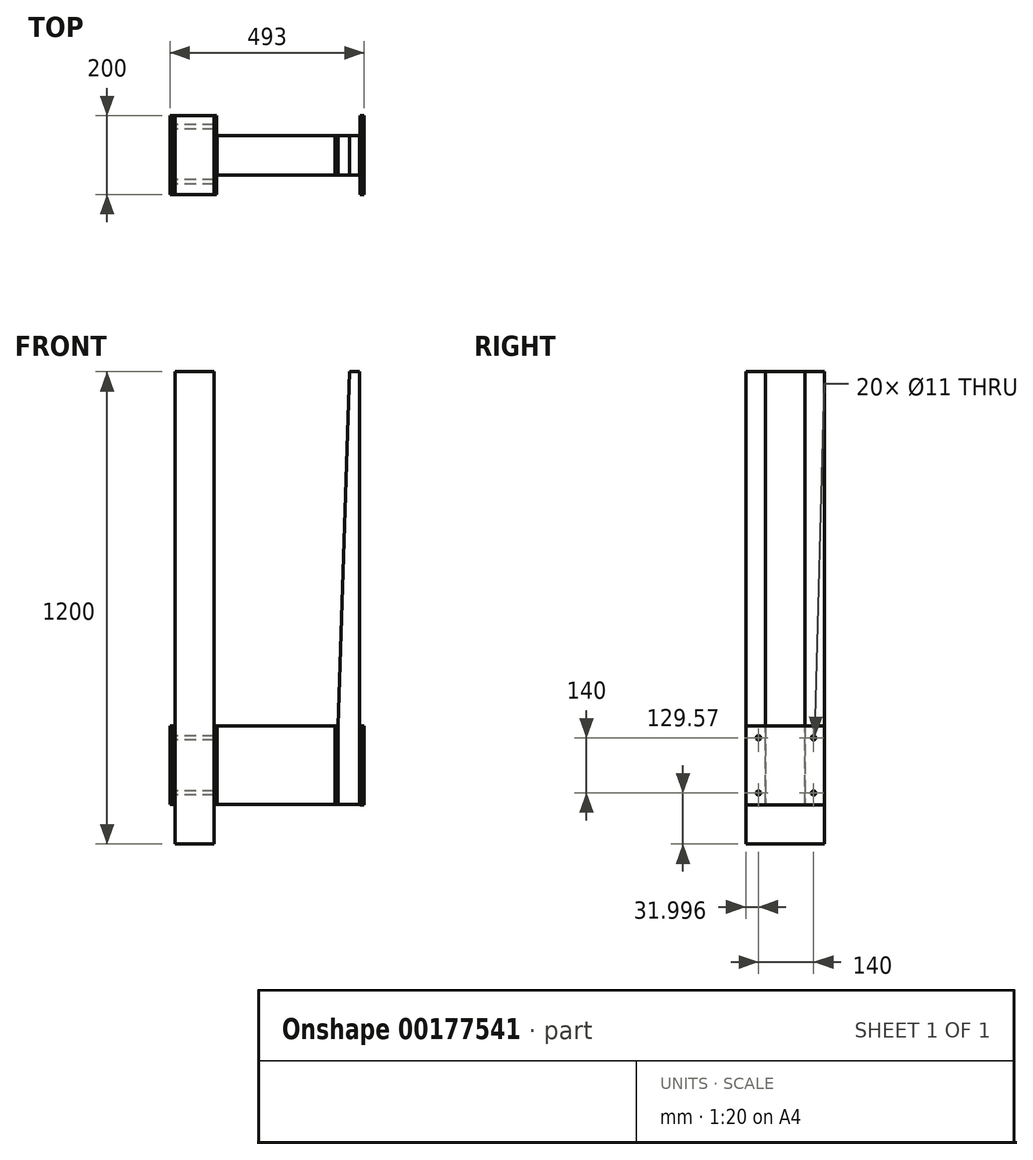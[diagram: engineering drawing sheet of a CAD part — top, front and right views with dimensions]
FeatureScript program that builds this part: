
annotation { "Feature Type Name" : "Feature", "Feature Type Description" : "" }
export const myFeature = defineFeature(function(context is Context, id is Id, definition is map)
    precondition{}
    {
        {
            var Q0;
            Q0=qCreatedBy(makeId("Front.planeOp"),FACE);
            var sketch = newSketch(context, id + "F0", { "sketchPlane" : qUnion([Q0])});
            skLineSegment(sketch, "E0", {"start": v(116.79, 818.01) * mm, "end": v(116.79, -281.99) * mm});
            skLineSegment(sketch, "E1", {"start": v(116.79, -281.99) * mm, "end": v(61.79, -281.99) * mm});
            skLineSegment(sketch, "E2", {"start": v(61.79, -281.99) * mm, "end": v(61.79, -81.99) * mm});
            skLineSegment(sketch, "E3", {"start": v(116.79, 818.01) * mm, "end": v(91.79, 818.01) * mm});
            skLineSegment(sketch, "E4", {"start": v(91.79, 818.01) * mm, "end": v(61.79, -81.99) * mm});
            skLineSegment(sketch, "E5.bottom", {"start": v(-245.21, -81.62) * mm, "end": v(54.79, -81.62) * mm});
            skLineSegment(sketch, "E5.top", {"start": v(-245.21, -281.62) * mm, "end": v(54.79, -281.62) * mm});
            skLineSegment(sketch, "E5.left", {"start": v(54.79, -81.62) * mm, "end": v(54.79, -281.62) * mm});
            skLineSegment(sketch, "E5.right", {"start": v(-245.21, -81.62) * mm, "end": v(-245.21, -281.62) * mm});
            skLineSegment(sketch, "E6.bottom", {"start": v(-352.21, 818.13) * mm, "end": v(-252.21, 818.13) * mm});
            skLineSegment(sketch, "E6.top", {"start": v(-352.21, -381.87) * mm, "end": v(-252.21, -381.87) * mm});
            skLineSegment(sketch, "E6.left", {"start": v(-352.21, 818.13) * mm, "end": v(-352.21, -381.87) * mm});
            skLineSegment(sketch, "E6.right", {"start": v(-252.21, 818.13) * mm, "end": v(-252.21, -381.87) * mm});
            skLineSegment(sketch, "E7.bottom", {"start": v(123.79, -82.45) * mm, "end": v(128.79, -82.45) * mm});
            skLineSegment(sketch, "E7.top", {"start": v(123.79, -282.45) * mm, "end": v(128.79, -282.45) * mm});
            skLineSegment(sketch, "E7.left", {"start": v(123.79, -82.45) * mm, "end": v(123.79, -282.45) * mm});
            skLineSegment(sketch, "E7.right", {"start": v(128.79, -82.45) * mm, "end": v(128.79, -282.45) * mm});
            skLineSegment(sketch, "E8.bottom", {"start": v(-364.21, -81.85) * mm, "end": v(-359.21, -81.85) * mm});
            skLineSegment(sketch, "E8.top", {"start": v(-364.21, -281.85) * mm, "end": v(-359.21, -281.85) * mm});
            skLineSegment(sketch, "E8.left", {"start": v(-364.21, -81.85) * mm, "end": v(-364.21, -281.85) * mm});
            skLineSegment(sketch, "E8.right", {"start": v(-359.21, -81.85) * mm, "end": v(-359.21, -281.85) * mm});
            skLineSegment(sketch, "E9.bottom", {"start": v(-358.21, -281.87) * mm, "end": v(-353.21, -281.87) * mm});
            skLineSegment(sketch, "E9.top", {"start": v(-358.21, -81.87) * mm, "end": v(-353.21, -81.87) * mm});
            skLineSegment(sketch, "E9.left", {"start": v(-358.21, -281.87) * mm, "end": v(-358.21, -81.87) * mm});
            skLineSegment(sketch, "E9.right", {"start": v(-353.21, -281.87) * mm, "end": v(-353.21, -81.87) * mm});
            skLineSegment(sketch, "E10.bottom", {"start": v(-251.21, -281.62) * mm, "end": v(-246.21, -281.62) * mm});
            skLineSegment(sketch, "E10.top", {"start": v(-251.21, -81.62) * mm, "end": v(-246.21, -81.62) * mm});
            skLineSegment(sketch, "E10.left", {"start": v(-251.21, -281.62) * mm, "end": v(-251.21, -81.62) * mm});
            skLineSegment(sketch, "E10.right", {"start": v(-246.21, -281.62) * mm, "end": v(-246.21, -81.62) * mm});
            skLineSegment(sketch, "E11.bottom", {"start": v(117.79, -82.45) * mm, "end": v(122.79, -82.45) * mm});
            skLineSegment(sketch, "E11.top", {"start": v(117.79, -282.45) * mm, "end": v(122.79, -282.45) * mm});
            skLineSegment(sketch, "E11.left", {"start": v(117.79, -82.45) * mm, "end": v(117.79, -282.45) * mm});
            skLineSegment(sketch, "E11.right", {"start": v(122.79, -82.45) * mm, "end": v(122.79, -282.45) * mm});
            skLineSegment(sketch, "E12.bottom", {"start": v(55.79, -81.99) * mm, "end": v(60.79, -81.99) * mm});
            skLineSegment(sketch, "E12.top", {"start": v(55.79, -281.99) * mm, "end": v(60.79, -281.99) * mm});
            skLineSegment(sketch, "E12.left", {"start": v(55.79, -81.99) * mm, "end": v(55.79, -281.99) * mm});
            skLineSegment(sketch, "E12.right", {"start": v(60.79, -81.99) * mm, "end": v(60.79, -281.99) * mm});
            skSolve(sketch);
        }
        {
            var Q0;
            Q0=makeQuery(id+"F0.imprint","IMPRINT",FACE,{"disambiguationData":[TD([[makeQuery(id+"F0.imprint","IMPRINT",EDGE,{"derivedFrom":sQuery(id+"F0.wireOp",EDGE,"E8.bottom")}),-1.0]])]});
            var Q1;
            Q1=makeQuery(id+"F0.imprint","IMPRINT",FACE,{"disambiguationData":[TD([[makeQuery(id+"F0.imprint","IMPRINT",EDGE,{"derivedFrom":sQuery(id+"F0.wireOp",EDGE,"E9.bottom")}),1.0]])]});
            var Q2;
            Q2=makeQuery(id+"F0.imprint","IMPRINT",FACE,{"disambiguationData":[TD([[makeQuery(id+"F0.imprint","IMPRINT",EDGE,{"derivedFrom":sQuery(id+"F0.wireOp",EDGE,"E6.bottom")}),-1.0]])]});
            var Q3;
            Q3=makeQuery(id+"F0.imprint","IMPRINT",FACE,{"disambiguationData":[TD([[makeQuery(id+"F0.imprint","IMPRINT",EDGE,{"derivedFrom":sQuery(id+"F0.wireOp",EDGE,"E10.bottom")}),1.0]])]});
            var Q4;
            Q4=makeQuery(id+"F0.imprint","IMPRINT",FACE,{"disambiguationData":[TD([[makeQuery(id+"F0.imprint","IMPRINT",EDGE,{"derivedFrom":sQuery(id+"F0.wireOp",EDGE,"E7.bottom")}),-1.0]])]});
            var Q5;
            Q5=makeQuery(id+"F0.imprint","IMPRINT",FACE,{"disambiguationData":[TD([[makeQuery(id+"F0.imprint","IMPRINT",EDGE,{"derivedFrom":sQuery(id+"F0.wireOp",EDGE,"E11.bottom")}),-1.0]])]});
            extrude(context, id + "F1", {"entities" : qUnion([Q0, Q1, Q2, Q3, Q4, Q5]), "endBound" : BoundingType.SYMMETRIC, "depth" : 200 * mm});
        }
        {
            var Q0;
            Q0=makeQuery(id+"F0.imprint","IMPRINT",FACE,{"disambiguationData":[TD([[makeQuery(id+"F0.imprint","IMPRINT",EDGE,{"derivedFrom":sQuery(id+"F0.wireOp",EDGE,"E5.bottom")}),-1.0]])]});
            var Q1;
            Q1=makeQuery(id+"F0.imprint","IMPRINT",FACE,{"disambiguationData":[TD([[makeQuery(id+"F0.imprint","IMPRINT",EDGE,{"derivedFrom":sQuery(id+"F0.wireOp",EDGE,"E12.bottom")}),-1.0]])]});
            var Q2;
            Q2=makeQuery(id+"F0.imprint","IMPRINT",FACE,{"disambiguationData":[TD([[makeQuery(id+"F0.imprint","IMPRINT",EDGE,{"derivedFrom":sQuery(id+"F0.wireOp",EDGE,"E0")}),-1.0]])]});
            extrude(context, id + "F2", {"entities" : qUnion([Q0, Q1, Q2]), "endBound" : BoundingType.SYMMETRIC, "depth" : 100 * mm});
        }
        {
            var Q0;
            Q0=makeQuery(id+"F1.opExtrude","SWEPT_FACE",FACE,{"disambiguationData":[OSD([sQuery(id+"F0.wireOp",EDGE,"E8.left")])]});
            var sketch = newSketch(context, id + "F3", { "sketchPlane" : qUnion([Q0])});
            skPoint(sketch, "E13.1.0.0", {"position": v(68, -112.3) * mm});
            skPoint(sketch, "E14.0.1.0", {"position": v(68, -252.3) * mm});
            skPoint(sketch, "E14.1.0.0", {"position": v(-72, -112.3) * mm});
            skPoint(sketch, "E14.1.1.0", {"position": v(-72, -252.3) * mm});
            skLineSegment(sketch, "E14.direction1", {"start": v(68, -112.3) * mm, "end": v(-72, -112.3) * mm, "construction": true});
            skLineSegment(sketch, "E14.direction2", {"start": v(68, -112.3) * mm, "end": v(68, -252.3) * mm, "construction": true});
            skSolve(sketch);
        }
        {
            var Q0;
            Q0=sQuery(id+"F3.wireOp",VERTEX,"E13.1.0.0");
            var Q1;
            Q1=sQuery(id+"F3.wireOp",VERTEX,"E14.1.0.0");
            var Q2;
            Q2=sQuery(id+"F3.wireOp",VERTEX,"E14.1.1.0");
            var Q3;
            Q3=sQuery(id+"F3.wireOp",VERTEX,"E14.0.1.0");
            var Q4;
            Q4=makeQuery(id+"F1.opExtrude","SWEPT_BODY",BODY,{"disambiguationData":[OSD([sQuery(id+"F0.wireOp",EDGE,"E7.bottom"),sQuery(id+"F0.wireOp",EDGE,"E7.top"),sQuery(id+"F0.wireOp",EDGE,"E7.left"),sQuery(id+"F0.wireOp",EDGE,"E7.right")])]});
            var Q5;
            Q5=makeQuery(id+"F1.opExtrude","SWEPT_BODY",BODY,{"disambiguationData":[OSD([sQuery(id+"F0.wireOp",EDGE,"E10.bottom"),sQuery(id+"F0.wireOp",EDGE,"E10.top"),sQuery(id+"F0.wireOp",EDGE,"E10.left"),sQuery(id+"F0.wireOp",EDGE,"E10.right")])]});
            var Q6;
            Q6=makeQuery(id+"F1.opExtrude","SWEPT_BODY",BODY,{"disambiguationData":[OSD([sQuery(id+"F0.wireOp",EDGE,"E6.bottom"),sQuery(id+"F0.wireOp",EDGE,"E6.top"),sQuery(id+"F0.wireOp",EDGE,"E6.left"),sQuery(id+"F0.wireOp",EDGE,"E6.right")])]});
            var Q7;
            Q7=makeQuery(id+"F1.opExtrude","SWEPT_BODY",BODY,{"disambiguationData":[OSD([sQuery(id+"F0.wireOp",EDGE,"E9.bottom"),sQuery(id+"F0.wireOp",EDGE,"E9.top"),sQuery(id+"F0.wireOp",EDGE,"E9.left"),sQuery(id+"F0.wireOp",EDGE,"E9.right")])]});
            var Q8;
            Q8=makeQuery(id+"F1.opExtrude","SWEPT_BODY",BODY,{"disambiguationData":[OSD([sQuery(id+"F0.wireOp",EDGE,"E8.bottom"),sQuery(id+"F0.wireOp",EDGE,"E8.top"),sQuery(id+"F0.wireOp",EDGE,"E8.left"),sQuery(id+"F0.wireOp",EDGE,"E8.right")])]});
            hole(context, id + "F4", {"style" : HoleStyle.SIMPLE, "endStyle" : HoleEndStyle.THROUGH, "standardTappedOrClearance" : lookupTablePath({ "standard" : "ISO", "fit" : "Normal", "size" : "M10", "type" : "Clearance" }), "standardBlindInLast" : lookupTablePath({ "fit" : "Standard", "standard" : "ISO", "size" : "M10", "type" : "Clearance" }), "holeDiameter" : 11 * mm, "locations" : qUnion([Q0, Q1, Q2, Q3]), "scope" : qUnion([Q4, Q5, Q6, Q7, Q8]), "tappedDepth" : 12 * mm, "tapClearance" : 3});
        }
    });
